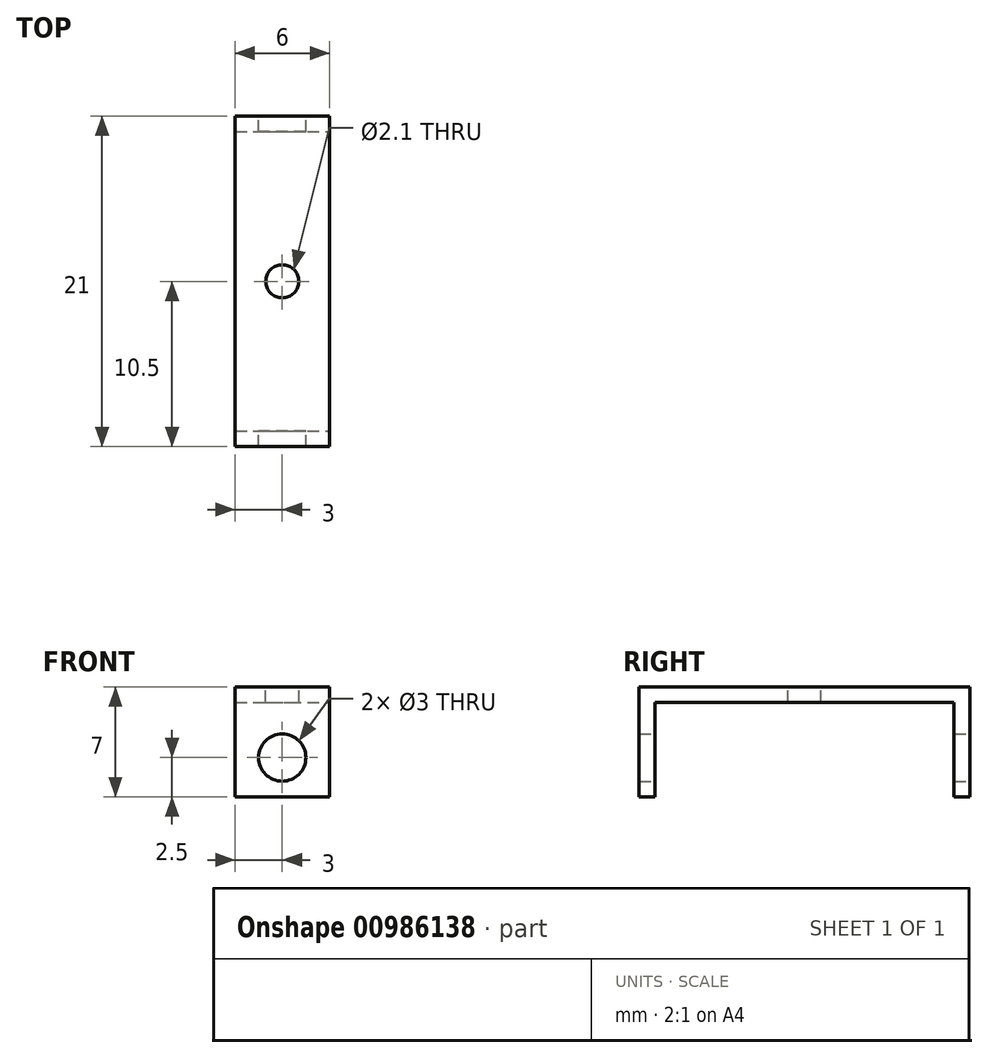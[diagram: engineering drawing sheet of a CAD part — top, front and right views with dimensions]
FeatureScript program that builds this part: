
annotation { "Feature Type Name" : "Feature", "Feature Type Description" : "" }
export const myFeature = defineFeature(function(context is Context, id is Id, definition is map)
    precondition{}
    {
        {
            var Q0;
            Q0=qCreatedBy(makeId("Front.planeOp"),FACE);
            var sketch = newSketch(context, id + "F0", { "sketchPlane" : qUnion([Q0])});
            skLineSegment(sketch, "E0", {"start": v(0, 0) * mm, "end": v(-6, 0) * mm});
            skLineSegment(sketch, "E1", {"start": v(-6, 0) * mm, "end": v(-6, -7) * mm});
            skLineSegment(sketch, "E2", {"start": v(-6, -7) * mm, "end": v(0, -7) * mm});
            skLineSegment(sketch, "E3", {"start": v(0, -7) * mm, "end": v(0, 0) * mm});
            skCircle(sketch, "E4", {"center": v(-3, -4.5) * mm, "radius": 1.5 * mm});
            skSolve(sketch);
        }
        {
            var Q0;
            Q0=makeQuery(id+"F0.imprint","IMPRINT",FACE,{"disambiguationData":[TD([[makeQuery(id+"F0.imprint","IMPRINT",EDGE,{"derivedFrom":sQuery(id+"F0.wireOp",EDGE,"E0")}),1.0]])]});
            extrude(context, id + "F1", {"entities" : qUnion([Q0]), "depth" : 21 * mm, "offsetDistance" : 25 * mm});
        }
        {
            var Q0;
            Q0=makeQuery(id+"F1.opExtrude","SWEPT_FACE",FACE,{"disambiguationData":[OSD([sQuery(id+"F0.wireOp",EDGE,"E3")])]});
            var sketch = newSketch(context, id + "F2", { "sketchPlane" : qUnion([Q0])});
            skLineSegment(sketch, "E5", {"start": v(-21, -7) * mm, "end": v(-20, -7) * mm});
            skLineSegment(sketch, "E6", {"start": v(-20, -7) * mm, "end": v(-20, -1) * mm});
            skLineSegment(sketch, "E7", {"start": v(-20, -1) * mm, "end": v(-1, -1) * mm});
            skLineSegment(sketch, "E8", {"start": v(-1, -1) * mm, "end": v(-1, -7) * mm});
            skSolve(sketch);
        }
        {
            var Q0;
            Q0 = qSketchRegion(id + "F2", true);
            var Q1;
            {var subQ0=sQuery(id+"F2.wireOp",EDGE,"E6");Q1=makeQuery(id+"F2.imprint","IMPRINT",FACE,{"disambiguationData":[TD([[makeQuery(id+"F2.imprint","IMPRINT",EDGE,{"derivedFrom":subQ0}),-1.0]])]});}
            extrude(context, id + "F3", {"entities" : qUnion([Q0, Q1]), "operationType" : NewBodyOperationType.REMOVE, "oppositeDirection" : true, "depth" : 10.4 * mm, "offsetDistance" : 25 * mm});
        }
        {
            var Q0;
            Q0=makeQuery(id+"F1.opExtrude","SWEPT_FACE",FACE,{"disambiguationData":[OSD([sQuery(id+"F0.wireOp",EDGE,"E0")])]});
            var sketch = newSketch(context, id + "F4", { "sketchPlane" : qUnion([Q0])});
            skCircle(sketch, "E9", {"center": v(-3, -10.5) * mm, "radius": 1.05 * mm});
            skSolve(sketch);
        }
        {
            var Q0;
            Q0=makeQuery(id+"F4.imprint","IMPRINT",FACE,{"disambiguationData":[TD([[makeQuery(id+"F4.imprint","IMPRINT",EDGE,{"derivedFrom":sQuery(id+"F4.wireOp",EDGE,"E9")}),1.0]])]});
            extrude(context, id + "F5", {"entities" : qUnion([Q0]), "operationType" : NewBodyOperationType.REMOVE, "oppositeDirection" : true, "depth" : 25 * mm, "offsetDistance" : 25 * mm});
        }
    });
